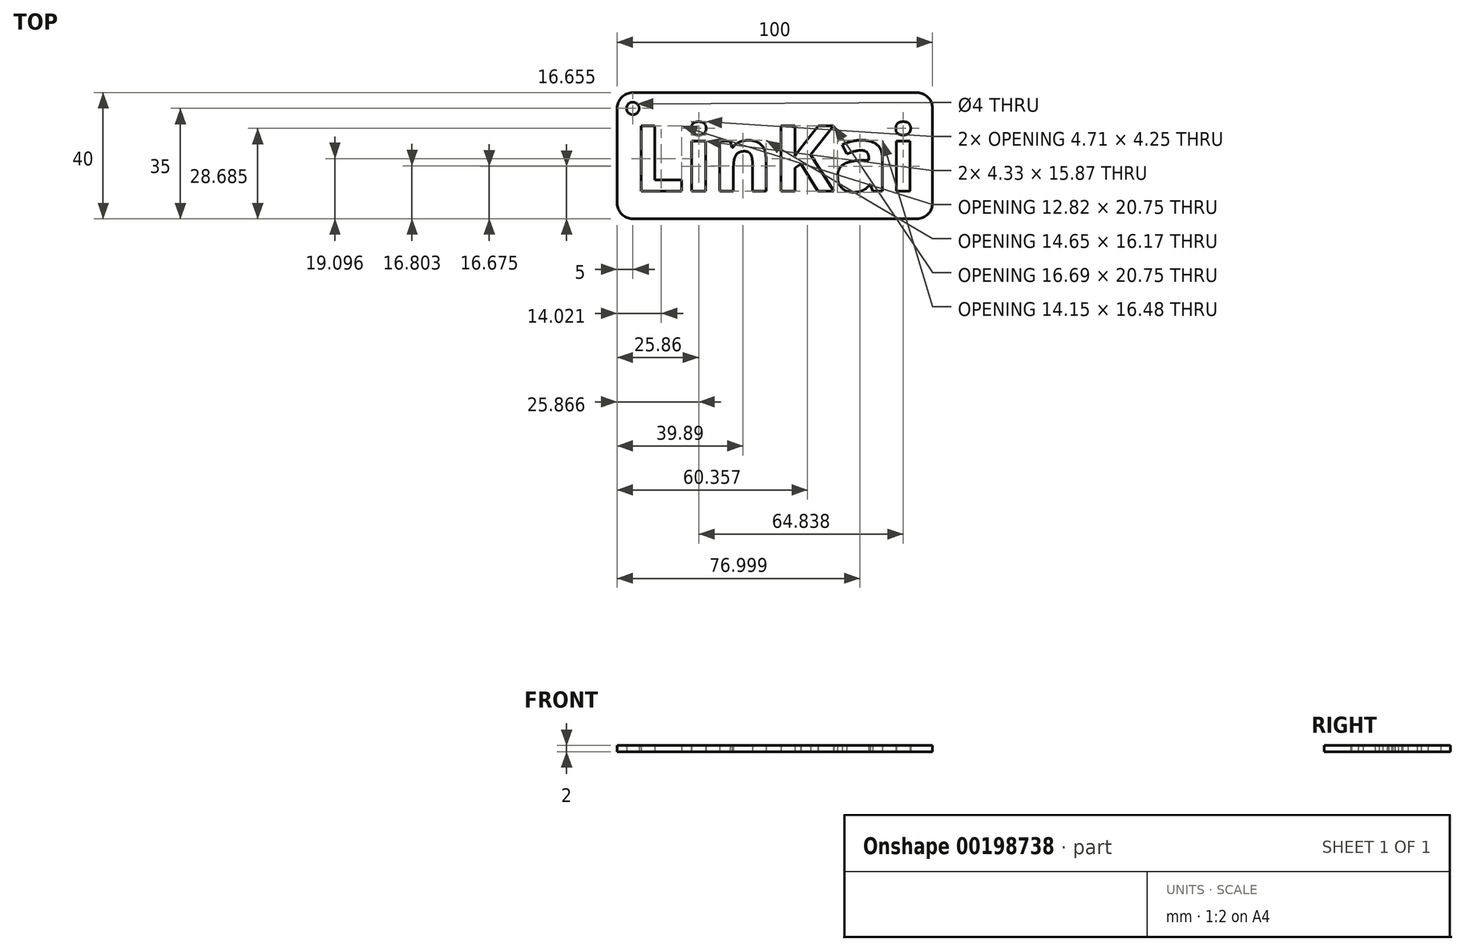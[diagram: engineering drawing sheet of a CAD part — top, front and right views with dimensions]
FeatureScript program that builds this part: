
annotation { "Feature Type Name" : "Feature", "Feature Type Description" : "" }
export const myFeature = defineFeature(function(context is Context, id is Id, definition is map)
    precondition{}
    {
        {
            var Q0;
            Q0=qCreatedBy(makeId("Top.planeOp"),FACE);
            var sketch = newSketch(context, id + "F0", { "sketchPlane" : qUnion([Q0])});
            skLineSegment(sketch, "E0.bottom", {"start": v(5, 0) * mm, "end": v(95, 0) * mm});
            skLineSegment(sketch, "E0.top", {"start": v(5, 40) * mm, "end": v(95, 40) * mm});
            skLineSegment(sketch, "E0.left", {"start": v(0, 5) * mm, "end": v(0, 35) * mm});
            skLineSegment(sketch, "E0.right", {"start": v(100, 5) * mm, "end": v(100, 35) * mm});
            skPoint(sketch, "E1.visualSharp", {"position": v(0, 40) * mm});
            skArc(sketch, "E1.filletArc", {"start": v(5, 40) * mm, "mid": v(1.46, 38.54) * mm, "end": v(0, 35) * mm});
            skPoint(sketch, "E2.visualSharp", {"position": v(0, 0) * mm});
            skArc(sketch, "E2.filletArc", {"start": v(0, 5) * mm, "mid": v(1.46, 1.46) * mm, "end": v(5, 0) * mm});
            skPoint(sketch, "E3.visualSharp", {"position": v(100, 0) * mm});
            skArc(sketch, "E3.filletArc", {"start": v(95, 0) * mm, "mid": v(98.54, 1.46) * mm, "end": v(100, 5) * mm});
            skPoint(sketch, "E4.visualSharp", {"position": v(100, 40) * mm});
            skArc(sketch, "E4.filletArc", {"start": v(100, 35) * mm, "mid": v(98.54, 38.54) * mm, "end": v(95, 40) * mm});
            skCircle(sketch, "E5", {"center": v(5, 35) * mm, "radius": 2 * mm});
            skText(sketch, "E6", { "text": "LinKai", "fontName": "OpenSans-Bold.ttf"});
            const initialGuessF0  = {"E6": [0.005, 0.00872, 1, 0, 0.02093]};
            skSetInitialGuess(sketch, initialGuessF0);
            skSolve(sketch);
        }
        {
            var Q0;
            Q0 = qSketchRegion(id + "F0", true);
            extrude(context, id + "F1", {"entities" : qUnion([Q0]), "depth" : 2 * mm});
        }
    });
